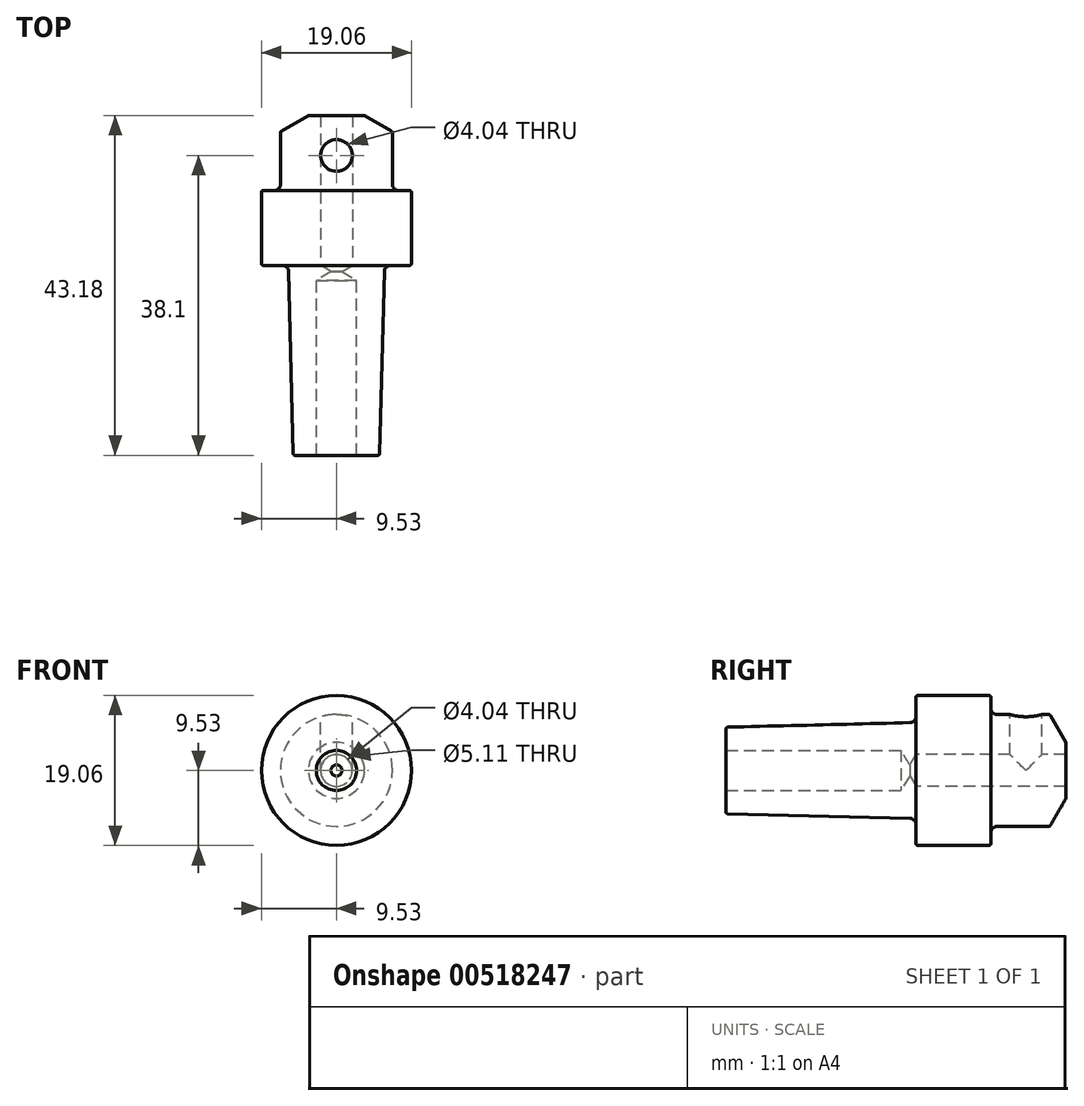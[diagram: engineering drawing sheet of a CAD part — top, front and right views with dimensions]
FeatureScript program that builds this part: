
annotation { "Feature Type Name" : "Feature", "Feature Type Description" : "" }
export const myFeature = defineFeature(function(context is Context, id is Id, definition is map)
    precondition{}
    {
        {
            var Q0;
            Q0=qCreatedBy(makeId("Right.planeOp"),FACE);
            var sketch = newSketch(context, id + "F0", { "sketchPlane" : qUnion([Q0])});
            skLineSegment(sketch, "E0", {"start": v(19.05, 0) * mm, "end": v(19.05, 9.53) * mm});
            skLineSegment(sketch, "E1", {"start": v(19.05, 9.53) * mm, "end": v(0, 9.53) * mm});
            skLineSegment(sketch, "E2", {"start": v(0, 9.53) * mm, "end": v(0, 6.1) * mm});
            skLineSegment(sketch, "E3", {"start": v(0, 6.1) * mm, "end": v(-24.13, 5.5) * mm});
            skLineSegment(sketch, "E4", {"start": v(-24.13, 5.5) * mm, "end": v(-24.13, 0) * mm});
            skLineSegment(sketch, "E5", {"start": v(-24.13, 0) * mm, "end": v(19.05, 0) * mm});
            skLineSegment(sketch, "E6", {"start": v(-54.58, 0) * mm, "end": v(70.03, 0) * mm, "construction": true});
            skSolve(sketch);
        }
        {
            var Q0;
            Q0=qSketchRegion(id+"F0",true);
            var Q1;
            Q1=sQuery(id+"F0.wireOp",EDGE,"E5");
            revolve(context, id + "F1", {"entities" : qUnion([Q0]), "axis" : qUnion([Q1]), "revolveType" : RevolveType.FULL});
        }
        {
            var Q0;
            Q0=makeQuery(id+"F1.opRevolve","SWEPT_FACE",FACE,{"disambiguationData":[OSD([sQuery(id+"F0.wireOp",EDGE,"E4")])]});
            var sketch = newSketch(context, id + "F2", { "sketchPlane" : qUnion([Q0])});
            skPoint(sketch, "E7", {"position": v(0, 0) * mm});
            skSolve(sketch);
        }
        {
            var Q0;
            Q0=sQuery(id+"F2.wireOp",VERTEX,"E7");
            var Q1;
            Q1=makeQuery(id+"F1.opRevolve","SWEPT_BODY",BODY,{"disambiguationData":[OSD([sQuery(id+"F0.wireOp",EDGE,"E0"),sQuery(id+"F0.wireOp",EDGE,"E1"),sQuery(id+"F0.wireOp",EDGE,"E2"),sQuery(id+"F0.wireOp",EDGE,"E3"),sQuery(id+"F0.wireOp",EDGE,"E4"),sQuery(id+"F0.wireOp",EDGE,"E5")])]});
            hole(context, id + "F3", {"style" : HoleStyle.SIMPLE, "endStyle" : HoleEndStyle.BLIND, "standardTappedOrClearance" : lookupTablePath({ "standard" : "ANSI", "engagement" : "75%", "pitch" : "20 tpi", "size" : "1/4", "type" : "Tapped" }), "standardBlindInLast" : lookupTablePath({ "standard" : "ANSI", "engagement" : "75%", "pitch" : "20 tpi", "size" : "1/4", "type" : "Tapped" }), "holeDiameter" : 5.1 * mm, "showTappedDepth" : true, "holeDepth" : 22.22 * mm, "isTappedThrough" : true, "tappedDepth" : 18.41 * mm, "tapClearance" : 3, "startFromSketch" : true, "locations" : qUnion([Q0]), "scope" : qUnion([Q1]), "majorDiameter" : 6.35 * mm});
        }
        {
            var Q0;
            Q0=makeQuery(id+"F1.opRevolve","SWEPT_EDGE",EDGE,{"disambiguationData":[OSD([sQuery(id+"F0.wireOp",EDGE,"E2"),sQuery(id+"F0.wireOp",EDGE,"E3")])]});
            fillet(context, id + "F4", {"entities" : qUnion([Q0]), "radius" : 0.76 * mm, "tangentPropagation" : true, "allowEdgeOverflow" : false});
        }
        {
            var Q0;
            Q0=makeQuery(id+"F1.opRevolve","SWEPT_EDGE",EDGE,{"disambiguationData":[OSD([sQuery(id+"F0.wireOp",EDGE,"E1"),sQuery(id+"F0.wireOp",EDGE,"E2")])]});
            var Q1;
            Q1=makeQuery(id+"F1.opRevolve","SWEPT_EDGE",EDGE,{"disambiguationData":[OSD([sQuery(id+"F0.wireOp",EDGE,"E0"),sQuery(id+"F0.wireOp",EDGE,"E1")])]});
            var Q2;
            Q2=makeQuery(id+"F1.opRevolve","SWEPT_EDGE",EDGE,{"disambiguationData":[OSD([sQuery(id+"F0.wireOp",EDGE,"E3"),sQuery(id+"F0.wireOp",EDGE,"E4")])]});
            fillet(context, id + "F5", {"entities" : qUnion([Q0, Q1, Q2]), "radius" : 0.25 * mm, "tangentPropagation" : true, "allowEdgeOverflow" : false});
        }
        {
            var Q0;
            Q0=makeQuery(id+"F1.opRevolve","SWEPT_FACE",FACE,{"disambiguationData":[OSD([sQuery(id+"F0.wireOp",EDGE,"E0")])]});
            var sketch = newSketch(context, id + "F6", { "sketchPlane" : qUnion([Q0])});
            skPoint(sketch, "E8", {"position": v(0, 0) * mm});
            skSolve(sketch);
        }
        {
            var Q0;
            Q0=sQuery(id+"F6.wireOp",VERTEX,"E8");
            var Q1;
            Q1=makeQuery(id+"F1.opRevolve","SWEPT_BODY",BODY,{"disambiguationData":[OSD([sQuery(id+"F0.wireOp",EDGE,"E0"),sQuery(id+"F0.wireOp",EDGE,"E1"),sQuery(id+"F0.wireOp",EDGE,"E2"),sQuery(id+"F0.wireOp",EDGE,"E3"),sQuery(id+"F0.wireOp",EDGE,"E4"),sQuery(id+"F0.wireOp",EDGE,"E5")])]});
            hole(context, id + "F7", {"style" : HoleStyle.SIMPLE, "endStyle" : HoleEndStyle.BLIND, "standardTappedOrClearance" : lookupTablePath({ "standard" : "ANSI", "size" : "#21 (0.16)", "type" : "Drilled" }), "standardBlindInLast" : lookupTablePath({ "standard" : "ANSI", "size" : "#21", "type" : "Drilled" }), "holeDiameter" : 4.04 * mm, "holeDepth" : 19.05 * mm, "isTappedThrough" : true, "tappedDepth" : 18.41 * mm, "tapClearance" : 3, "startFromSketch" : true, "locations" : qUnion([Q0]), "scope" : qUnion([Q1])});
        }
        {
            var Q0;
            Q0=qCreatedBy(makeId("Right.planeOp"),FACE);
            var sketch = newSketch(context, id + "F8", { "sketchPlane" : qUnion([Q0])});
            skLineSegment(sketch, "E9", {"start": v(9.52, 25.4) * mm, "end": v(9.53, 7.11) * mm});
            skLineSegment(sketch, "E10", {"start": v(9.53, 7.11) * mm, "end": v(17, 7.11) * mm});
            skLineSegment(sketch, "E11", {"start": v(17, 7.11) * mm, "end": v(19.05, 3.56) * mm});
            skLineSegment(sketch, "E12", {"start": v(19.05, 3.56) * mm, "end": v(19.05, 25.4) * mm});
            skLineSegment(sketch, "E13", {"start": v(19.05, 25.4) * mm, "end": v(9.52, 25.4) * mm});
            skLineSegment(sketch, "E14", {"start": v(41.63, 0) * mm, "end": v(-30.36, 0) * mm, "construction": true});
            skSolve(sketch);
        }
        {
            var Q0;
            Q0 = qSketchRegion(id + "F8", true);
            var Q1;
            Q1=sQuery(id+"F8.wireOp",EDGE,"E14");
            revolve(context, id + "F9", {"operationType" : NewBodyOperationType.REMOVE, "entities" : qUnion([Q0]), "axis" : qUnion([Q1]), "revolveType" : RevolveType.FULL, "oppositeDirection" : true});
        }
        {
            var Q0;
            Q0=makeQuery(id+"F9.boolean.opBoolean","COPY",EDGE,{"derivedFrom":makeQuery(id+"F9.opRevolve","SWEPT_EDGE",EDGE,{"disambiguationData":[OSD([sQuery(id+"F8.wireOp",EDGE,"E9"),sQuery(id+"F8.wireOp",EDGE,"E10")])]})});
            fillet(context, id + "F10", {"entities" : qUnion([Q0]), "radius" : 0.76 * mm, "tangentPropagation" : true, "allowEdgeOverflow" : false});
        }
        {
            var Q0;
            Q0=makeQuery(id+"F9.boolean.opBoolean","INTERSECT",EDGE,{"derivedFrom":[makeQuery(id+"F1.opRevolve","SWEPT_FACE",FACE,{"disambiguationData":[OSD([sQuery(id+"F0.wireOp",EDGE,"E1")])]}),makeQuery(id+"F9.opRevolve","SWEPT_FACE",FACE,{"disambiguationData":[OSD([sQuery(id+"F8.wireOp",EDGE,"E9")])]})]});
            var Q1;
            Q1=makeQuery(id+"F9.boolean.opBoolean","COPY",EDGE,{"derivedFrom":makeQuery(id+"F9.opRevolve","SWEPT_EDGE",EDGE,{"disambiguationData":[OSD([sQuery(id+"F8.wireOp",EDGE,"E10"),sQuery(id+"F8.wireOp",EDGE,"E11")])]})});
            var Q2;
            Q2=makeQuery(id+"F9.boolean.opBoolean","COPY",EDGE,{"derivedFrom":makeQuery(id+"F9.opRevolve","SWEPT_EDGE",EDGE,{"disambiguationData":[OSD([sQuery(id+"F8.wireOp",EDGE,"E11"),sQuery(id+"F8.wireOp",EDGE,"E12")])]})});
            fillet(context, id + "F11", {"entities" : qUnion([Q0, Q1, Q2]), "radius" : 0.25 * mm, "tangentPropagation" : true, "allowEdgeOverflow" : false});
        }
        {
            var Q0;
            Q0=qCreatedBy(makeId("Top.planeOp"),FACE);
            var sketch = newSketch(context, id + "F12", { "sketchPlane" : qUnion([Q0])});
            skPoint(sketch, "E15", {"position": v(0, 13.97) * mm});
            skSolve(sketch);
        }
        {
            var Q0;
            Q0=sQuery(id+"F12.wireOp",VERTEX,"E15");
            var Q1;
            Q1=makeQuery(id+"F1.opRevolve","SWEPT_BODY",BODY,{"disambiguationData":[OSD([sQuery(id+"F0.wireOp",EDGE,"E0"),sQuery(id+"F0.wireOp",EDGE,"E1"),sQuery(id+"F0.wireOp",EDGE,"E2"),sQuery(id+"F0.wireOp",EDGE,"E3"),sQuery(id+"F0.wireOp",EDGE,"E4"),sQuery(id+"F0.wireOp",EDGE,"E5")])]});
            hole(context, id + "F13", {"style" : HoleStyle.SIMPLE, "endStyle" : HoleEndStyle.BLIND, "oppositeDirection" : true, "standardTappedOrClearance" : lookupTablePath({ "standard" : "ANSI", "engagement" : "75%", "pitch" : "32 tpi", "size" : "#10", "type" : "Tapped" }), "standardBlindInLast" : lookupTablePath({ "standard" : "ANSI", "engagement" : "75%", "pitch" : "32 tpi", "size" : "#10", "type" : "Tapped" }), "holeDiameter" : 4.04 * mm, "showTappedDepth" : true, "holeDepth" : 20.8 * mm, "isTappedThrough" : true, "tappedDepth" : 18.41 * mm, "tapClearance" : 3, "startFromSketch" : true, "locations" : qUnion([Q0]), "scope" : qUnion([Q1]), "majorDiameter" : 4.83 * mm});
        }
    });
